# Revit family: Weitspannkabelrinne gelocht, Boden gesickt
name_source: partatom
category: Generic Models
revit_build: Autodesk Revit 2015 (Build: 20140606_1530(x64)
units: mm (PartAtom-declared; Revit-internal decimal feet)

## types (10) — shared parameters
Lenght = 6000 mm  [stored 19.685 ft]
Manufacturer = OBO Bettermann
Material = Steel, Galvanized
URL = http://www.obo-bettermann.com

## per-type parameters (varying)
| type | GTIN | Manufacturer Art.No. | Width |
| WKSG 120 FS | 4012196351435 | 6098111 | 200 mm  [stored 0.656168 ft] |
| WKSG 130 FS | 4012196351497 | 6098115 | 300 mm |
| WKSG 140 FS | 4012196351558 | 6098119 | 400 mm  [stored 1.31234 ft] |
| WKSG 150 FS | 4012196351619 | 6098123 | 500 mm  [stored 1.64042 ft] |
| WKSG 160 FS | 4012196351671 | 6098127 | 600 mm  [stored 1.9685 ft] |
| WKSG 120 FT | 4012196351732 | 6098141 | 200 mm  [stored 0.656168 ft] |
| WKSG 130 FT | 4012196370030 | 6098145 | 300 mm |
| WKSG 140 FT | 4012196034277 | 6098149 | 400 mm  [stored 1.31234 ft] |
| WKSG 150 FT | 4012196034031 | 6098153 | 500 mm  [stored 1.64042 ft] |
| WKSG 160 FT | 4012196033973 | 6098157 | 600 mm  [stored 1.9685 ft] |

note: column(s) folded — value = type name in every type: Article Type

note: [stored X ft] marks values corroborated as IEEE doubles in the binary element streams (Revit-internal decimal feet)

## geometry (parser evidence)
native form markers: Sweep x4
no freeform markers — native parametric forms only
